# Revit family: ВентКлиматСтрой Вентилятор дымоудаления крышный радиальный ВКР
name_source: partatom
category: Оборудование
units: mm (PartAtom-declared; Revit-internal decimal feet)

## family parameters
Всегда вертикально = Да
Заголовок OmniClass = Fans for Air Ductwork
На основе рабочей плоскости = Нет
Номер OmniClass = 23.75.35.17.11
Общий = Нет
При загрузке вырезать с полостями = Нет
Размер круглого соединителя = Использовать диаметр
Тип детали = Нормальный
Точка расчета площади = Да

## types (12) — shared parameters
ADSK_Версия Revit = 2019
ADSK_Версия семейства = rev.1
ADSK_Единица измерения = шт.
ADSK_Классификация нагрузок = Прочее
ADSK_Количество = 1
ADSK_Количество фаз числовое = 3
ADSK_Напряжение = 380 В
ADSK_Предел огнестойкости = 120
ADSK_Предел огнестойкости экземпляра = 120 мин.
Data = ВКР
Poles = 3
Описание = Вентилятор дымоудаления крышный радиальный с выходом потока вверх
УГО_3D = Да
zero-valued in all types: ADSK_Материал тип подсчета

## per-type parameters (varying)
| type | A | B | B1 | D | E | E1 | H | H1 | H1' | H2 | H3 | STM_A | STM_B | STM_C | ang | b | d | h | w | МинРазмерШахты |
| ВКР-3,55ДУ | 450 мм | 595 мм | 535 мм | 355 мм | 650 мм | 304 мм | 630 мм | 284 мм | 249 мм | 95 мм | 189 мм | 520 мм | 685 мм | 420 мм | 75.21° | 30 мм | 11 мм | 35 мм | 107 мм | 500 мм |
| ВКР-4ДУ | 450 мм | 595 мм | 535 мм | 400 мм | 650 мм | 271 мм | 690 мм | 311 мм | 276 мм | 104 мм | 207 мм | 565 мм | 730 мм | 465 мм | 76.60° | 30 мм | 11 мм | 35 мм | 107 мм | 545 мм |
| ВКР-4,5ДУ | 535 мм | 665 мм | 605 мм | 450 мм | 700 мм | 260 мм | 800 мм | 360 мм | 320 мм | 120 мм | 240 мм | 615 мм | 780 мм | 515 мм | 80.38° | 30 мм | 11 мм | 40 мм | 121 мм | 595 мм |
| ВКР-5ДУ | 535 мм | 665 мм | 605 мм | 500 мм | 700 мм | 288 мм | 750 мм | 338 мм | 298 мм | 113 мм | 225 мм | 665 мм | 830 мм | 565 мм | 79.67° | 30 мм | 11 мм | 40 мм | 121 мм | 645 мм |
| ВКР-5,6ДУ | 750 мм | 940 мм | 880 мм | 560 мм | 950 мм | 455 мм | 900 мм | 405 мм | 365 мм | 135 мм | 270 мм | 725 мм | 890 мм | 625 мм | 84.52° | 40 мм | 13 мм | 40 мм | 150 мм | 705 мм |
| ВКР-6,3ДУ | 750 мм | 940 мм | 880 мм | 630 мм | 950 мм | 455 мм | 900 мм | 405 мм | 365 мм | 135 мм | 270 мм | 790 мм | 960 мм | 695 мм | 84.52° | 40 мм | 13 мм | 40 мм | 150 мм | 775 мм |
| ВКР-7,1ДУ | 840 мм | 1010 мм | 950 мм | 710 мм | 1025 мм | 459 мм | 1030 мм | 464 мм | 414 мм | 150 мм | 309 мм | 875 мм | 1040 мм | 775 мм | 84.82° | 40 мм | 13 мм | 50 мм | 150 мм | 855 мм |
| ВКР-8ДУ | 1050 мм | 1250 мм | 1190 мм | 800 мм | 1350 мм | 709 мм | 1165 мм | 524 мм | 474 мм | 150 мм | 350 мм | 1050 мм | 1210 мм | 865 мм | 80.43° | 40 мм | 16 мм | 50 мм | 150 мм | 945 мм |
| ВКР-9ДУ | 1050 мм | 1250 мм | 1190 мм | 900 мм | 1350 мм | 663 мм | 1250 мм | 563 мм | 513 мм | 150 мм | 375 мм | 1090 мм | 1230 мм | 965 мм | 81.13° | 40 мм | 16 мм | 50 мм | 150 мм | 1045 мм |
| ВКР-10ДУ | 1150 мм | 1350 мм | 1290 мм | 1000 мм | 1580 мм | 744 мм | 1520 мм | 684 мм | 634 мм | 150 мм | 456 мм | 1260 мм | 1420 мм | 1065 мм | 77.12° | 40 мм | 18 мм | 50 мм | 150 мм | 1145 мм |
| ВКР-11,2ДУ | 1150 мм | 1350 мм | 1290 мм | 1120 мм | 1580 мм | 744 мм | 1520 мм | 684 мм | 634 мм | 150 мм | 456 мм | 1390 мм | 1450 мм | 1185 мм | 77.12° | 40 мм | 18 мм | 50 мм | 150 мм | 1265 мм |
| ВКР-12,5ДУ | 1264 мм | 1464 мм | 1404 мм | 1250 мм | 1700 мм | 782 мм | 1670 мм | 752 мм | 702 мм | 150 мм | 501 мм | 1545 мм | 1700 мм | 1360 мм | 78.09° | 40 мм | 18 мм | 50 мм | 150 мм | 1395 мм |
